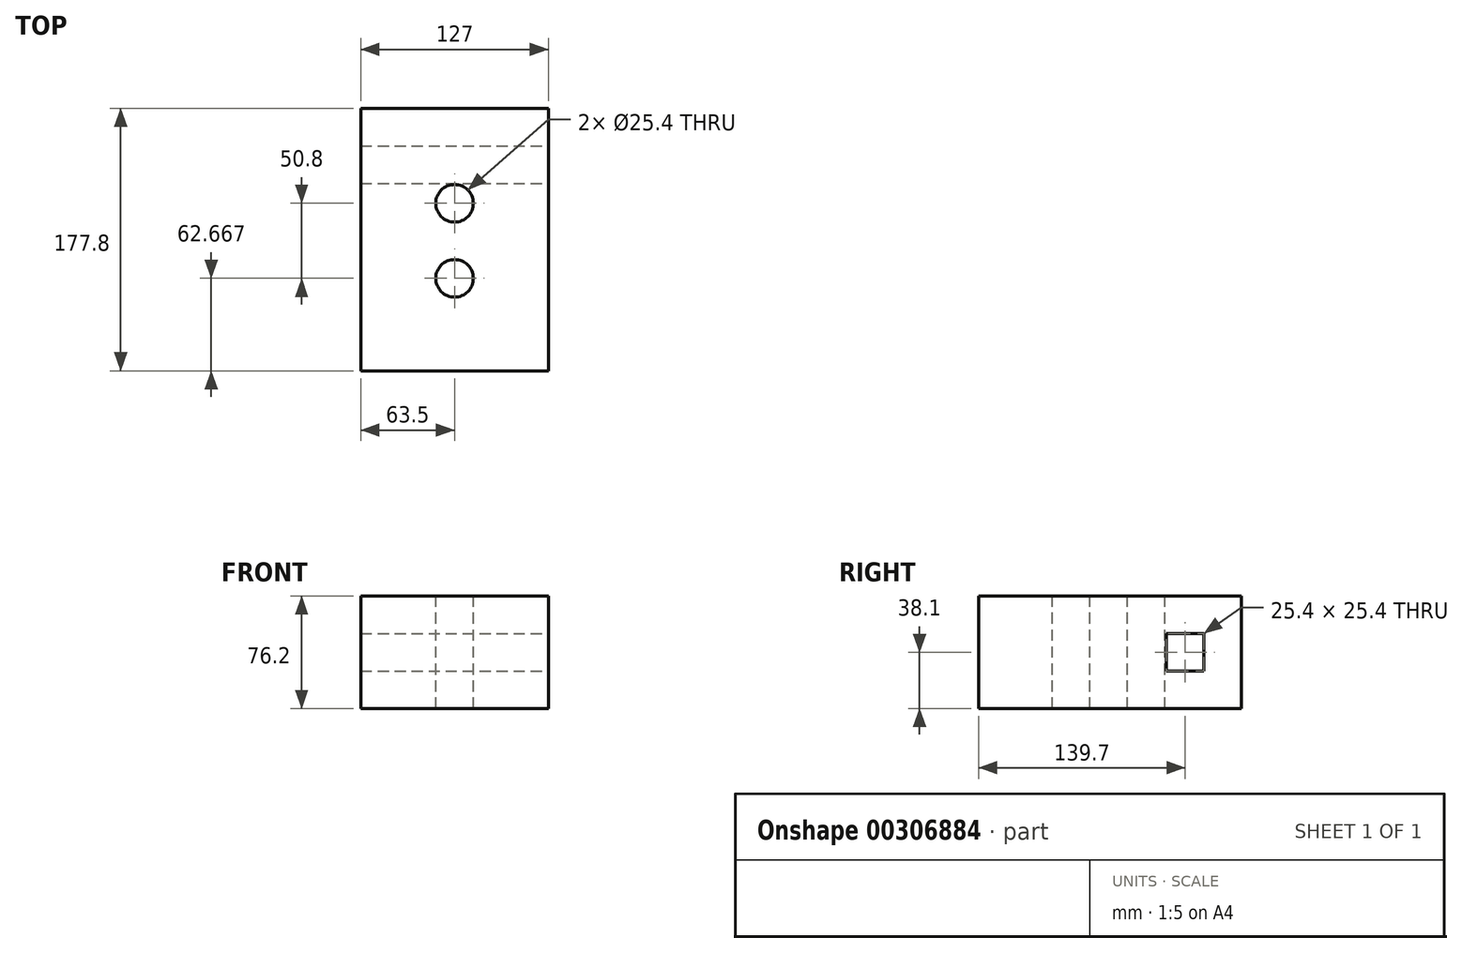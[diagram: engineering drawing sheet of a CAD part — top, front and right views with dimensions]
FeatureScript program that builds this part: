
annotation { "Feature Type Name" : "Feature", "Feature Type Description" : "" }
export const myFeature = defineFeature(function(context is Context, id is Id, definition is map)
    precondition{}
    {
        {
            var Q0;
            Q0=qCreatedBy(makeId("Top.planeOp"),FACE);
            var sketch = newSketch(context, id + "F0", { "sketchPlane" : qUnion([Q0])});
            skLineSegment(sketch, "E0.bottom", {"start": v(63.5, 88.9) * mm, "end": v(-63.5, 88.9) * mm});
            skLineSegment(sketch, "E0.top", {"start": v(63.5, -88.9) * mm, "end": v(-63.5, -88.9) * mm});
            skLineSegment(sketch, "E0.left", {"start": v(63.5, 88.9) * mm, "end": v(63.5, -88.9) * mm});
            skLineSegment(sketch, "E0.right", {"start": v(-63.5, 88.9) * mm, "end": v(-63.5, -88.9) * mm});
            skPoint(sketch, "E0.middle", {"position": v(0, 0) * mm});
            skSolve(sketch);
        }
        {
            var Q0;
            Q0=makeQuery(id+"F0.imprint","IMPRINT",FACE,{"disambiguationData":[TD([[makeQuery(id+"F0.imprint","IMPRINT",EDGE,{"derivedFrom":sQuery(id+"F0.wireOp",EDGE,"E0.bottom")}),1.0]])]});
            extrude(context, id + "F1", {"entities" : qUnion([Q0]), "endBound" : BoundingType.SYMMETRIC, "depth" : 76.2 * mm});
        }
        {
            var Q0;
            Q0=makeQuery(id+"F1.opExtrude","CAP_FACE",FACE,{"disambiguationData":[OSD([sQuery(id+"F0.wireOp",EDGE,"E0.bottom"),sQuery(id+"F0.wireOp",EDGE,"E0.top"),sQuery(id+"F0.wireOp",EDGE,"E0.left"),sQuery(id+"F0.wireOp",EDGE,"E0.right")])],"isStart":false});
            var sketch = newSketch(context, id + "F2", { "sketchPlane" : qUnion([Q0])});
            skCircle(sketch, "E1", {"center": v(0, 24.57) * mm, "radius": 12.7 * mm});
            skCircle(sketch, "E2", {"center": v(0, -26.23) * mm, "radius": 12.7 * mm});
            skSolve(sketch);
        }
        {
            var Q0;
            Q0=makeQuery(id+"F2.imprint","IMPRINT",FACE,{"disambiguationData":[TD([[makeQuery(id+"F2.imprint","IMPRINT",EDGE,{"derivedFrom":sQuery(id+"F2.wireOp",EDGE,"E1")}),1.0]])]});
            var Q1;
            Q1=makeQuery(id+"F2.imprint","IMPRINT",FACE,{"disambiguationData":[TD([[makeQuery(id+"F2.imprint","IMPRINT",EDGE,{"derivedFrom":sQuery(id+"F2.wireOp",EDGE,"E2")}),1.0]])]});
            extrude(context, id + "F3", {"entities" : qUnion([Q0, Q1]), "operationType" : NewBodyOperationType.REMOVE, "endBound" : BoundingType.THROUGH_ALL, "oppositeDirection" : true, "depth" : 25.4 * mm});
        }
        {
            var Q0;
            Q0=makeQuery(id+"F1.opExtrude","SWEPT_FACE",FACE,{"disambiguationData":[OSD([sQuery(id+"F0.wireOp",EDGE,"E0.left")])]});
            var sketch = newSketch(context, id + "F4", { "sketchPlane" : qUnion([Q0])});
            skLineSegment(sketch, "E3.bottom", {"start": v(38.1, -12.7) * mm, "end": v(63.5, -12.7) * mm});
            skLineSegment(sketch, "E3.top", {"start": v(38.1, 12.7) * mm, "end": v(63.5, 12.7) * mm});
            skLineSegment(sketch, "E3.left", {"start": v(38.1, -12.7) * mm, "end": v(38.1, 12.7) * mm});
            skLineSegment(sketch, "E3.right", {"start": v(63.5, -12.7) * mm, "end": v(63.5, 12.7) * mm});
            skPoint(sketch, "E3.middle", {"position": v(50.8, 0) * mm});
            skSolve(sketch);
        }
        {
            var Q0;
            Q0=makeQuery(id+"F4.imprint","IMPRINT",FACE,{"disambiguationData":[TD([[makeQuery(id+"F4.imprint","IMPRINT",EDGE,{"derivedFrom":sQuery(id+"F4.wireOp",EDGE,"E3.bottom")}),1.0]])]});
            extrude(context, id + "F5", {"entities" : qUnion([Q0]), "operationType" : NewBodyOperationType.REMOVE, "endBound" : BoundingType.THROUGH_ALL, "oppositeDirection" : true, "depth" : 25.4 * mm});
        }
    });
